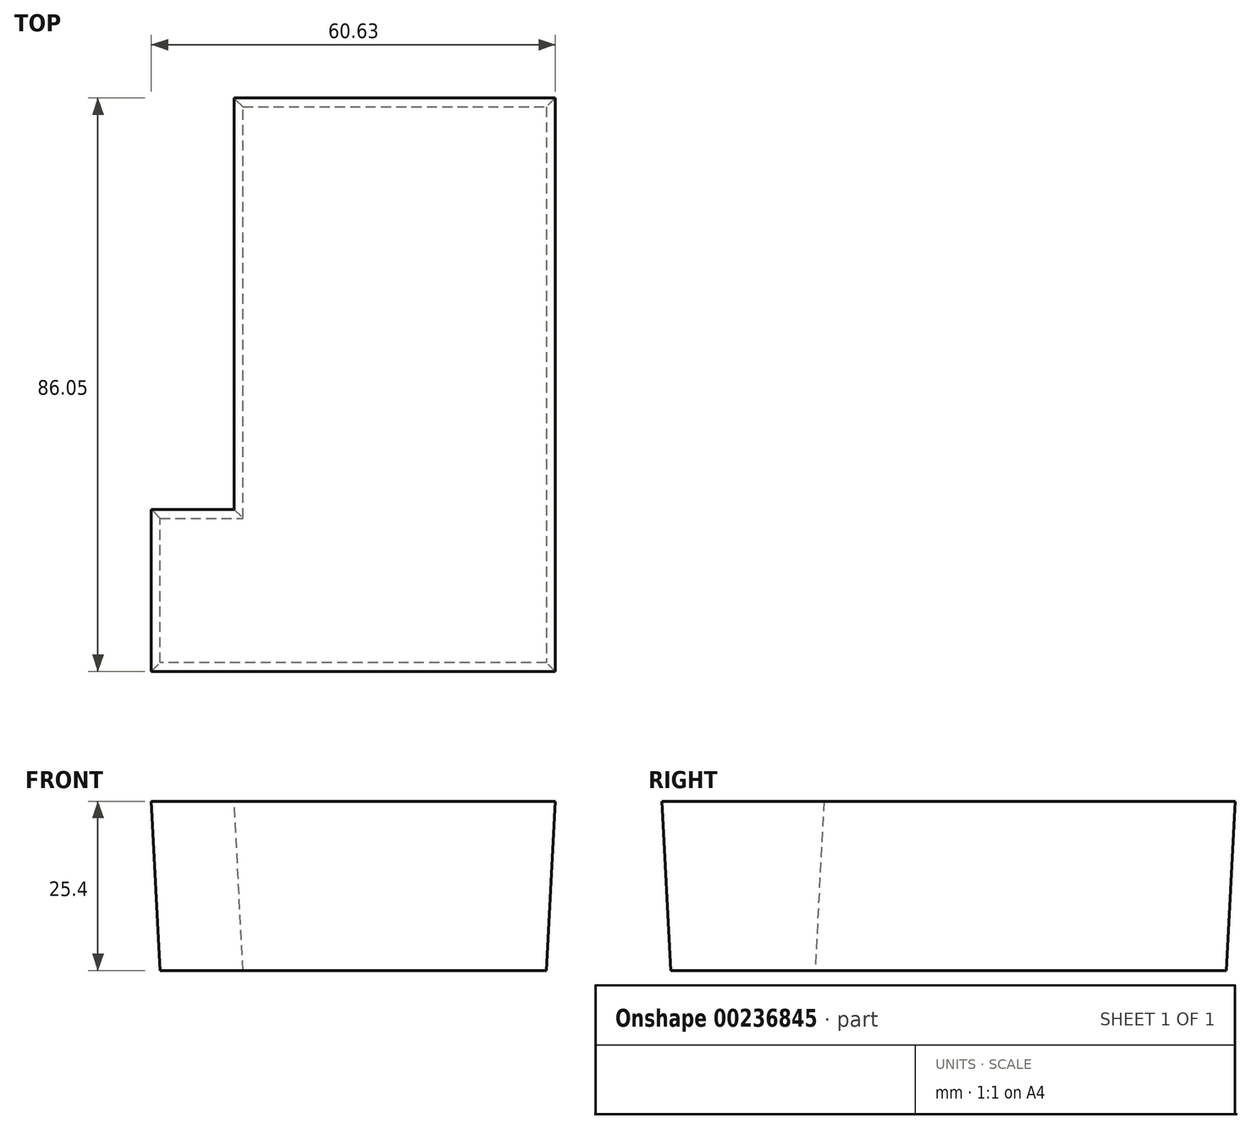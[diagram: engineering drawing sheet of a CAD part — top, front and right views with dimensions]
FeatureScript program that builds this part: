
annotation { "Feature Type Name" : "Feature", "Feature Type Description" : "" }
export const myFeature = defineFeature(function(context is Context, id is Id, definition is map)
    precondition{}
    {
        {
            var Q0;
            Q0=qCreatedBy(makeId("Top.planeOp"),FACE);
            var sketch = newSketch(context, id + "F0", { "sketchPlane" : qUnion([Q0])});
            skLineSegment(sketch, "E0.bottom", {"start": v(12.44, 61.74) * mm, "end": v(57.97, 61.74) * mm});
            skLineSegment(sketch, "E0.top", {"start": v(12.44, -21.65) * mm, "end": v(57.97, -21.65) * mm});
            skLineSegment(sketch, "E0.left", {"start": v(12.44, 61.74) * mm, "end": v(12.44, 0) * mm});
            skLineSegment(sketch, "E0.right", {"start": v(57.97, 61.74) * mm, "end": v(57.97, -21.65) * mm});
            skLineSegment(sketch, "E1.bottom", {"start": v(12.44, -21.65) * mm, "end": v(0, -21.65) * mm});
            skLineSegment(sketch, "E1.top", {"start": v(12.44, 0) * mm, "end": v(0, 0) * mm});
            skLineSegment(sketch, "E1.right", {"start": v(0, -21.65) * mm, "end": v(0, 0) * mm});
            skSolve(sketch);
        }
        {
            var Q0;
            Q0 = qSketchRegion(id + "F0", true);
            extrude(context, id + "F1", {"entities" : qUnion([Q0]), "depth" : 25.4 * mm, "hasDraft" : true, "draftAngle" : 3 * degree});
        }
    });
